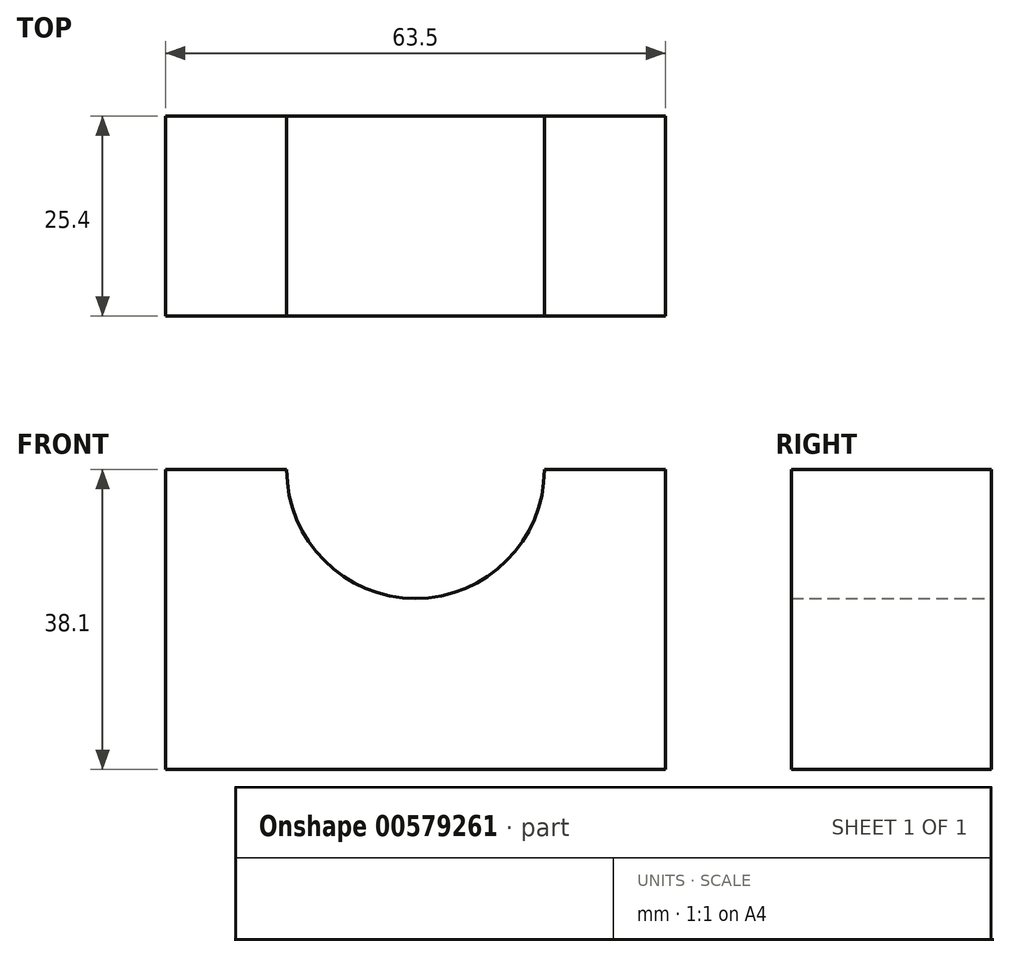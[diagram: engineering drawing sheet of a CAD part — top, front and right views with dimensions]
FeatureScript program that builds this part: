
annotation { "Feature Type Name" : "Feature", "Feature Type Description" : "" }
export const myFeature = defineFeature(function(context is Context, id is Id, definition is map)
    precondition{}
    {
        {
            var Q0;
            Q0=qCreatedBy(makeId("Front.planeOp"),FACE);
            var sketch = newSketch(context, id + "F0", { "sketchPlane" : qUnion([Q0])});
            skLineSegment(sketch, "E0", {"start": v(0, 0) * mm, "end": v(63.5, 0) * mm});
            skLineSegment(sketch, "E1", {"start": v(63.5, 0) * mm, "end": v(63.5, 38.1) * mm});
            skLineSegment(sketch, "E2", {"start": v(63.5, 38.1) * mm, "end": v(0, 38.1) * mm});
            skLineSegment(sketch, "E3", {"start": v(0, 38.1) * mm, "end": v(0, 0) * mm});
            skCircle(sketch, "E4", {"center": v(31.75, 38.1) * mm, "radius": 16.37 * mm});
            skSolve(sketch);
        }
        {
            var Q0;
            Q0=makeQuery(id+"F0.imprint","IMPRINT",FACE,{"disambiguationData":[TD([[makeQuery(id+"F0.imprint","IMPRINT",EDGE,{"derivedFrom":sQuery(id+"F0.wireOp",EDGE,"E0")}),1.0]])]});
            extrude(context, id + "F1", {"entities" : qUnion([Q0]), "depth" : 25.4 * mm, "offsetDistance" : 25.4 * mm});
        }
    });
